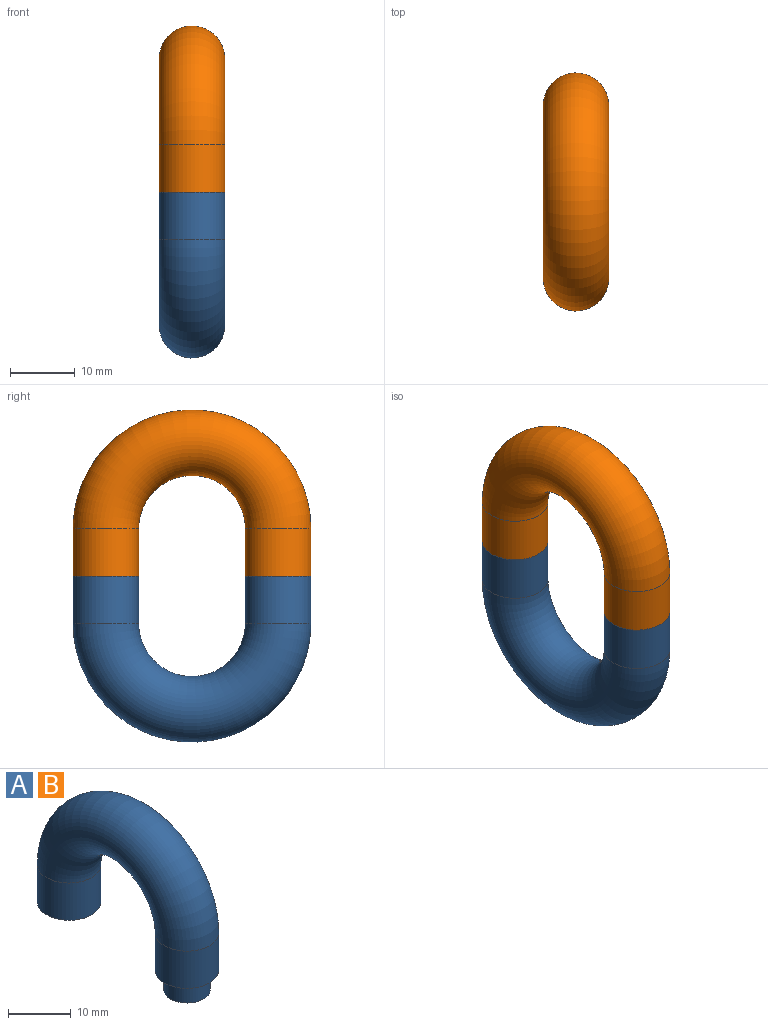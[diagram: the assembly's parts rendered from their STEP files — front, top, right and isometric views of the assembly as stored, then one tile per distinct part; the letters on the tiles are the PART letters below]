
ASSEMBLY  parts=2 mates=1
PART A: 15 faces, bbox 11.1x39.9x31 mm
  f0: torus R=13.33mm, axis (-1,0,0), area 1337.2mm2, adj f2,f4
  f1: plane 10.16x10.16mm, normal (0,0,-1), area 15.4mm2, adj f2,f14
  f2: cylinder r=5.08mm len=10.16mm, axis (0,0,1), area 233.1mm2, adj f0,f1
  f3: plane 10.16x10.16mm, normal (0,0,-1), area 17.6mm2, adj f4,f13
  f4: cylinder r=5.08mm len=10.16mm, axis (0,0,1), area 233.1mm2, adj f0,f3
  f5: torus R=13.33mm, axis (-1,0,0), area 1002.9mm2, adj f6,f7
  f6: cylinder r=3.81mm len=7.62mm, axis (0,0,1), area 156.6mm2, adj f5,f14
  f7: cylinder r=3.81mm len=7.62mm, axis (0,0,1), area 30.9mm2, adj f5,f11
  f8: cylinder r=2.54mm len=5.61mm, axis (0,0,-1), area 89.5mm2, adj f10,f12
  f9: cylinder r=3.73mm len=7.47mm, axis (0,0,-1), area 71.5mm2, adj f10,f13
  f10: plane 7.47x7.47mm, normal (0,0,-1), area 23.5mm2, adj f8,f9
  f11: torus R=1.27mm, axis (0,0,-1), area 34.3mm2, adj f7,f12
  f12: torus R=7.62mm, axis (0,0,-1), area 52.8mm2, adj f8,f11
  f13: torus R=4.5mm, axis (0,0,1), area 30.2mm2, adj f3,f9
  f14: torus R=4.57mm, axis (0,0,1), area 30.7mm2, adj f1,f6
PART B: same geometry as A
PLACE A rot(axis=(1,0,0),180deg) t=(-6.76,-57.93,-18.49)mm
PLACE B t=(-6.76,39.44,-18.49)mm
MATE fastened A.f2 <-> B.f4  axis (0,0,1) through (-6.76,-22.58,-18.49)mm
